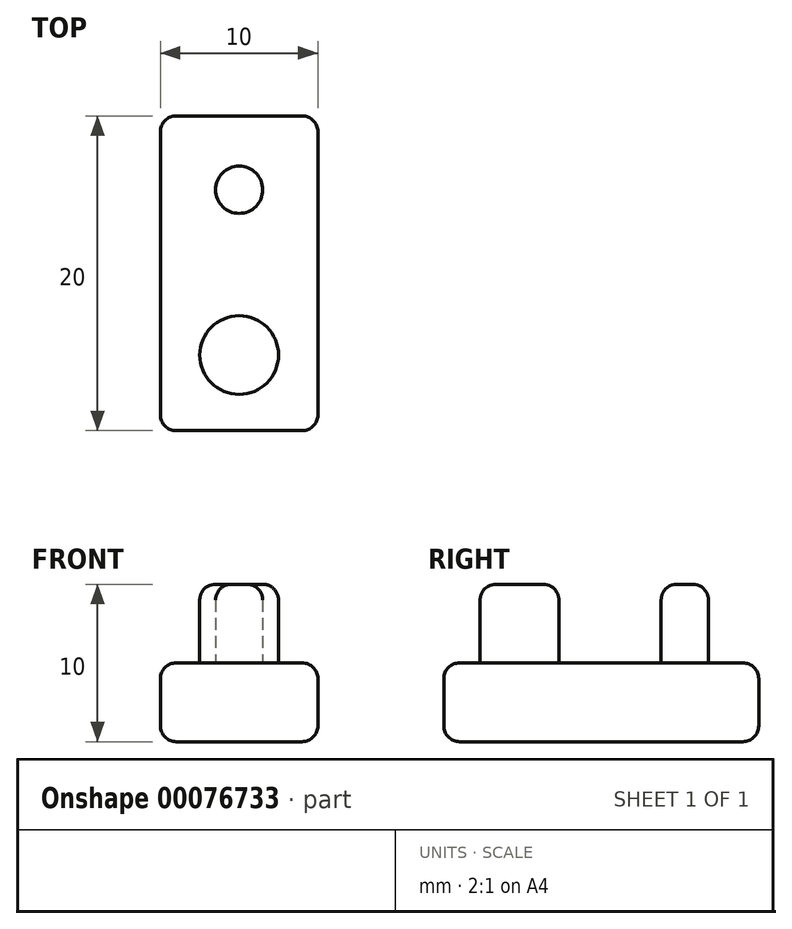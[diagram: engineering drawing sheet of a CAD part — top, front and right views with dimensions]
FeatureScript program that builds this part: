
annotation { "Feature Type Name" : "Feature", "Feature Type Description" : "" }
export const myFeature = defineFeature(function(context is Context, id is Id, definition is map)
    precondition{}
    {
        {
            var Q0;
            Q0=qCreatedBy(makeId("Top.planeOp"),FACE);
            var sketch = newSketch(context, id + "F0", { "sketchPlane" : qUnion([Q0])});
            skLineSegment(sketch, "E0.bottom", {"start": v(5, 10) * mm, "end": v(-5, 10) * mm});
            skLineSegment(sketch, "E0.top", {"start": v(5, -10) * mm, "end": v(-5, -10) * mm});
            skLineSegment(sketch, "E0.left", {"start": v(5, 10) * mm, "end": v(5, -10) * mm});
            skLineSegment(sketch, "E0.right", {"start": v(-5, 10) * mm, "end": v(-5, -10) * mm});
            skPoint(sketch, "E0.middle", {"position": v(0, 0) * mm});
            skSolve(sketch);
        }
        {
            var Q0;
            Q0 = qSketchRegion(id + "F0", true);
            extrude(context, id + "F1", {"entities" : qUnion([Q0]), "depth" : 5 * mm});
        }
        {
            var Q0;
            Q0=makeQuery(id+"F1.opExtrude","CAP_FACE",FACE,{"disambiguationData":[OSD([sQuery(id+"F0.wireOp",EDGE,"E0.bottom"),sQuery(id+"F0.wireOp",EDGE,"E0.top"),sQuery(id+"F0.wireOp",EDGE,"E0.left"),sQuery(id+"F0.wireOp",EDGE,"E0.right")])],"isStart":false});
            var sketch = newSketch(context, id + "F2", { "sketchPlane" : qUnion([Q0])});
            skCircle(sketch, "E1", {"center": v(0, 5.3) * mm, "radius": 1.5 * mm});
            skCircle(sketch, "E2", {"center": v(0, -5.2) * mm, "radius": 2.5 * mm});
            skPoint(sketch, "E2.centerSnap0", {"position": v(0, -10) * mm});
            skSolve(sketch);
        }
        {
            var Q0;
            Q0 = qSketchRegion(id + "F2", true);
            extrude(context, id + "F3", {"entities" : qUnion([Q0]), "operationType" : NewBodyOperationType.ADD, "depth" : 5 * mm});
        }
        {
            var Q0;
            Q0=makeQuery(id+"F1.opExtrude","CAP_EDGE",EDGE,{"disambiguationData":[OSD([sQuery(id+"F0.wireOp",EDGE,"E0.left")])],"isStart":false});
            var Q1;
            Q1=makeQuery(id+"F1.opExtrude","CAP_EDGE",EDGE,{"disambiguationData":[OSD([sQuery(id+"F0.wireOp",EDGE,"E0.top")])],"isStart":false});
            var Q2;
            Q2=makeQuery(id+"F1.opExtrude","SWEPT_FACE",FACE,{"disambiguationData":[OSD([sQuery(id+"F0.wireOp",EDGE,"E0.left")])]});
            var Q3;
            Q3=makeQuery(id+"F1.opExtrude","CAP_EDGE",EDGE,{"disambiguationData":[OSD([sQuery(id+"F0.wireOp",EDGE,"E0.right")])],"isStart":false});
            var Q4;
            Q4=makeQuery(id+"F1.opExtrude","CAP_EDGE",EDGE,{"disambiguationData":[OSD([sQuery(id+"F0.wireOp",EDGE,"E0.bottom")])],"isStart":false});
            var Q5;
            Q5=makeQuery(id+"F1.opExtrude","CAP_EDGE",EDGE,{"disambiguationData":[OSD([sQuery(id+"F0.wireOp",EDGE,"E0.top")])],"isStart":true});
            var Q6;
            Q6=makeQuery(id+"F1.opExtrude","CAP_EDGE",EDGE,{"disambiguationData":[OSD([sQuery(id+"F0.wireOp",EDGE,"E0.bottom")])],"isStart":true});
            var Q7;
            Q7=makeQuery(id+"F1.opExtrude","CAP_EDGE",EDGE,{"disambiguationData":[OSD([sQuery(id+"F0.wireOp",EDGE,"E0.right")])],"isStart":true});
            var Q8;
            Q8=makeQuery(id+"F1.opExtrude","SWEPT_EDGE",EDGE,{"disambiguationData":[OSD([sQuery(id+"F0.wireOp",EDGE,"E0.top"),sQuery(id+"F0.wireOp",EDGE,"E0.right")])]});
            var Q9;
            Q9=makeQuery(id+"F1.opExtrude","SWEPT_FACE",FACE,{"disambiguationData":[OSD([sQuery(id+"F0.wireOp",EDGE,"E0.bottom")])]});
            var Q10;
            Q10=makeQuery(id+"F3.opExtrude","CAP_EDGE",EDGE,{"disambiguationData":[OSD([sQuery(id+"F2.wireOp",EDGE,"E2")])],"isStart":false});
            var Q11;
            Q11=makeQuery(id+"F3.opExtrude","CAP_EDGE",EDGE,{"disambiguationData":[OSD([sQuery(id+"F2.wireOp",EDGE,"E1")])],"isStart":false});
            var Q12;
            Q12=makeQuery(id+"F3.opExtrude","CAP_EDGE",EDGE,{"disambiguationData":[OSD([sQuery(id+"F2.wireOp",EDGE,"E1")])],"isStart":true});
            var Q13;
            Q13=makeQuery(id+"F3.opExtrude","CAP_EDGE",EDGE,{"disambiguationData":[OSD([sQuery(id+"F2.wireOp",EDGE,"E2")])],"isStart":true});
            fillet(context, id + "F4", {"entities" : qUnion([Q0, Q1, Q2, Q3, Q4, Q5, Q6, Q7, Q8, Q9, Q10, Q11, Q12, Q13]), "radius" : 1 * mm, "tangentPropagation" : true, "allowEdgeOverflow" : false});
        }
    });
